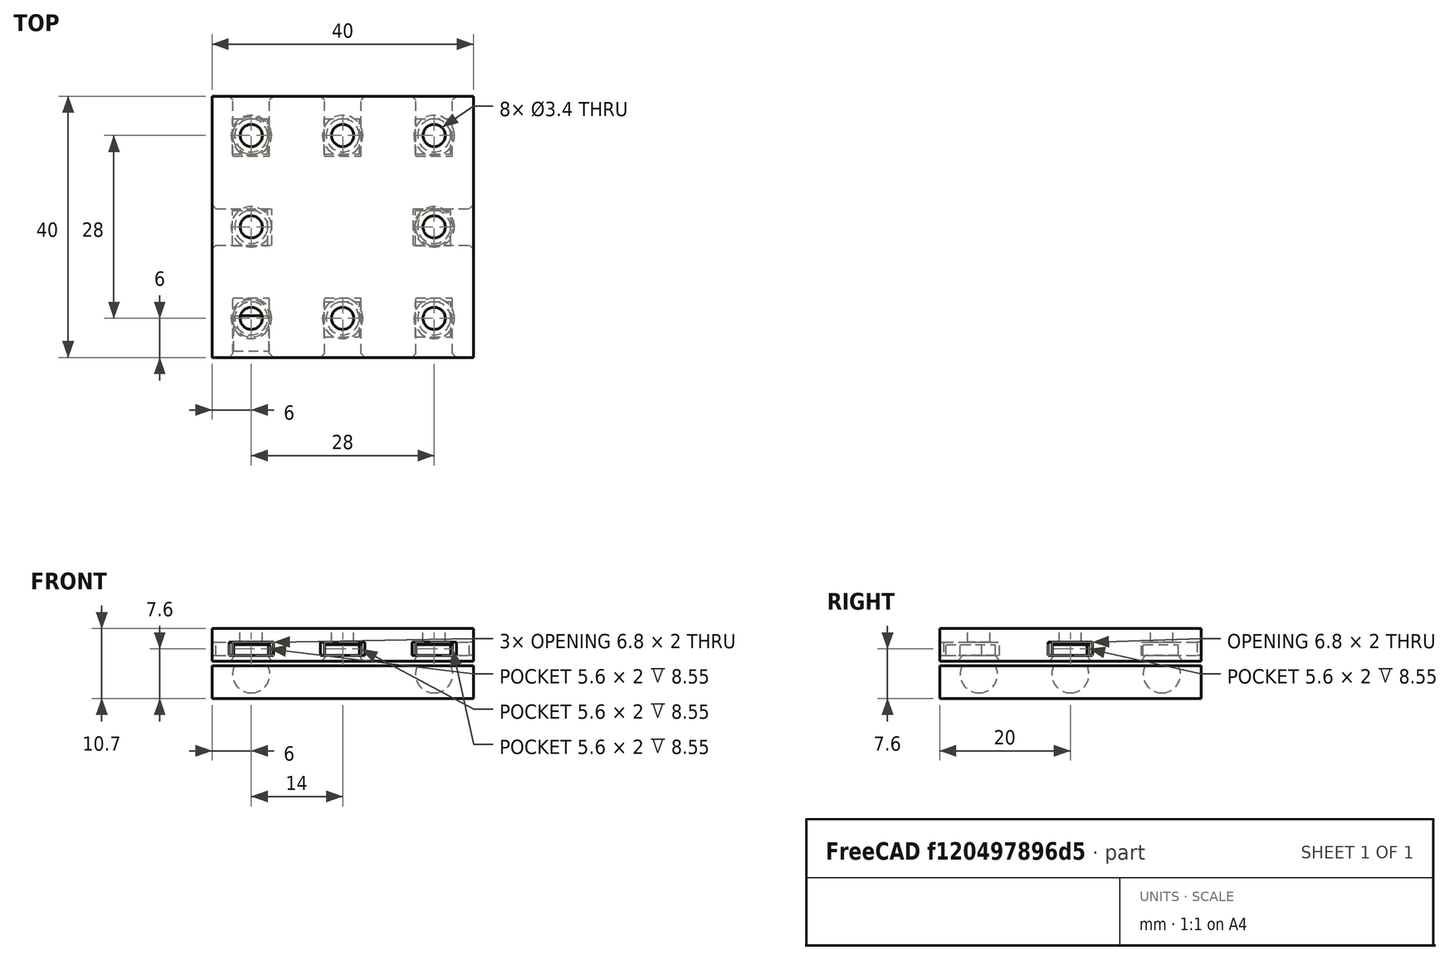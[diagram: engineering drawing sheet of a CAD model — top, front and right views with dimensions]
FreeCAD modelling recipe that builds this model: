
FCSTD DOCUMENT  (FreeCAD 0.17R13522 (Git))
Label: Face plates
License: All rights reserved
LicenseURL: http://en.wikipedia.org/wiki/All_rights_reserved
objects: Part::Box×18, Part::Sphere×11, Part::Cylinder×8, Part::MultiFuse×5, Part::Cut×4, Part::Chamfer×4
note: 50 computed .brp shape members not serialized (recipe doc carries the construction recipe); baked Part::Feature solids carry a one-line shape summary decoded from their .brp

FEATURE [Part::Box] Box  label="Cube"
  AttacherType = Attacher::AttachEngine3D
  Height = 5
  Length = 40
  Placement = pos=(0,0,-2) rot=(0,0,1;0rad)
  Width = 40
FEATURE [Part::Sphere] Sphere  label="Mag Hole"
  Angle1 = -90
  Angle2 = 90
  Angle3 = 360
  AttacherType = Attacher::AttachEngine3D
  Placement = pos=(6,6,1.7) rot=(0,0,1;0rad)
  Radius = 2.85
FEATURE [Part::Sphere] Sphere005  label="Mag Hole 2"
  Angle1 = -90
  Angle2 = 90
  Angle3 = 360
  AttacherType = Attacher::AttachEngine3D
  Placement = pos=(34,20,1.7) rot=(0,0,1;0rad)
  Radius = 2.85
FEATURE [Part::Sphere] Sphere003  label="Mag Hole 3"
  Angle1 = -90
  Angle2 = 90
  Angle3 = 360
  AttacherType = Attacher::AttachEngine3D
  Placement = pos=(6,34,1.7) rot=(0,0,1;0rad)
  Radius = 2.85
FEATURE [Part::Box] Box001  label="Cube001"
  AttacherType = Attacher::AttachEngine3D
  Height = 5
  Length = 40
  Placement = pos=(0,0,3.7) rot=(0,0,1;0rad)
  Width = 40
FEATURE [Part::Box] Box002  label="Square Nut"
  AttacherType = Attacher::AttachEngine3D
  Height = 1.65
  Length = 5.4
  Placement = pos=(3.3,1,4.6) rot=(0,0,1;0rad)
  Width = 5.4
FEATURE [Part::Box] Box003  label="Square Nut001"
  AttacherType = Attacher::AttachEngine3D
  Height = 1.65
  Length = 5.4
  Placement = pos=(31.15,17.15,4.6) rot=(0,0,1;0rad)
  Width = 5.4
FEATURE [Part::Box] Box005  label="Square Nut002"
  AttacherType = Attacher::AttachEngine3D
  Height = 1.65
  Length = 5.4
  Placement = pos=(3.15,31.15,4.6) rot=(0,0,1;0rad)
  Width = 5.4
FEATURE [Part::Box] Box006  label="Square Nut003"
  AttacherType = Attacher::AttachEngine3D
  Height = 1.65
  Length = 5.4
  Placement = pos=(17.15,3.15,4.6) rot=(0,0,1;0rad)
  Width = 5.4
FEATURE [Part::Box] Box007  label="Square Nut004"
  AttacherType = Attacher::AttachEngine3D
  Height = 1.65
  Length = 5.4
  Placement = pos=(17.15,31.15,4.6) rot=(0,0,1;0rad)
  Width = 5.4
FEATURE [Part::Box] Box008  label="Square Nut005"
  AttacherType = Attacher::AttachEngine3D
  Height = 1.65
  Length = 5.4
  Placement = pos=(31.15,3.15,4.6) rot=(0,0,1;0rad)
  Width = 5.4
FEATURE [Part::Box] Box009  label="Square Nut006"
  AttacherType = Attacher::AttachEngine3D
  Height = 1.65
  Length = 5.4
  Placement = pos=(31.15,31.15,4.6) rot=(0,0,1;0rad)
  Width = 5.4
FEATURE [Part::Box] Box010  label="Square Nut007"
  AttacherType = Attacher::AttachEngine3D
  Height = 1.65
  Length = 5.4
  Placement = pos=(3.15,17.15,4.6) rot=(0,0,1;0rad)
  Width = 5.4
FEATURE [Part::MultiFuse] Fusion  label="Square Nuts"
  Shapes = -> [Box008,Box007,Box006,Box003,Box005,Box009,Box010,Box002]
FEATURE [Part::Box] Box011  label="Square Nut Hole 008"
  AttacherType = Attacher::AttachEngine3D
  Height = 2
  Length = 5.6
  Placement = pos=(17.2,30.85,4.6) rot=(0,0,1;0rad)
  Width = 10
FEATURE [Part::Box] Box012  label="Square Nut Hole 009"
  AttacherType = Attacher::AttachEngine3D
  Height = 2
  Length = 5.6
  Placement = pos=(17.2,-0.85,4.6) rot=(0,0,1;0rad)
  Width = 10
FEATURE [Part::Box] Box013  label="Square Nut Hole 010"
  AttacherType = Attacher::AttachEngine3D
  Height = 2
  Length = 5.6
  Placement = pos=(31.2,-0.85,4.6) rot=(0,0,1;0rad)
  Width = 10
FEATURE [Part::Box] Box014  label="Square Nut Hole 011"
  AttacherType = Attacher::AttachEngine3D
  Height = 2
  Length = 10
  Placement = pos=(30.85,17.2,4.6) rot=(0,0,1;0rad)
  Width = 5.6
FEATURE [Part::Box] Box015  label="Square Nut Hole 012"
  AttacherType = Attacher::AttachEngine3D
  Height = 2
  Length = 5.6
  Placement = pos=(3.2,30.85,4.6) rot=(0,0,1;0rad)
  Width = 10
FEATURE [Part::Box] Box016  label="Square Nut Hole 013"
  AttacherType = Attacher::AttachEngine3D
  Height = 2
  Length = 5.6
  Placement = pos=(31.2,30.85,4.6) rot=(0,0,1;0rad)
  Width = 10
FEATURE [Part::Box] Box017  label="Square Nut Hole 014"
  AttacherType = Attacher::AttachEngine3D
  Height = 2
  Length = 10
  Placement = pos=(-0.85,17.2,4.6) rot=(0,0,1;0rad)
  Width = 5.6
FEATURE [Part::Box] Box018  label="Square Nut Hole 015"
  AttacherType = Attacher::AttachEngine3D
  Height = 2
  Length = 5.6
  Placement = pos=(3.2,-0.85,4.6) rot=(0,0,1;0rad)
  Width = 10
FEATURE [Part::MultiFuse] Fusion001  label="Square Nut Hole"
  Shapes = -> [Box013,Box014,Box016,Box012,Box017,Box015,Box018,Box011]
FEATURE [Part::Sphere] Sphere006  label="Nut Clearence1"
  Angle1 = -90
  Angle2 = 90
  Angle3 = 360
  AttacherType = Attacher::AttachEngine3D
  Placement = pos=(6,6,2.4) rot=(0,0,1;0rad)
  Radius = 3.35
FEATURE [Part::Sphere] Sphere007
  Angle1 = -90
  Angle2 = 90
  Angle3 = 360
  AttacherType = Attacher::AttachEngine3D
  Placement = pos=(34,20,2.4) rot=(0,0,1;0rad)
  Radius = 3.35
FEATURE [Part::Sphere] Sphere008
  Angle1 = -90
  Angle2 = 90
  Angle3 = 360
  AttacherType = Attacher::AttachEngine3D
  Placement = pos=(6,34,2.4) rot=(0,0,1;0rad)
  Radius = 3.35
FEATURE [Part::Sphere] Sphere001
  Angle1 = -90
  Angle2 = 90
  Angle3 = 360
  AttacherType = Attacher::AttachEngine3D
  Placement = pos=(34,6,2.4) rot=(0,0,1;0rad)
  Radius = 3.35
FEATURE [Part::Sphere] Sphere009
  Angle1 = -90
  Angle2 = 90
  Angle3 = 360
  AttacherType = Attacher::AttachEngine3D
  Placement = pos=(20,6,2.4) rot=(0,0,1;0rad)
  Radius = 3.35
FEATURE [Part::Sphere] Sphere010
  Angle1 = -90
  Angle2 = 90
  Angle3 = 360
  AttacherType = Attacher::AttachEngine3D
  Placement = pos=(20,34,2.4) rot=(0,0,1;0rad)
  Radius = 3.35
FEATURE [Part::Sphere] Sphere004
  Angle1 = -90
  Angle2 = 90
  Angle3 = 360
  AttacherType = Attacher::AttachEngine3D
  Placement = pos=(6,20,2.4) rot=(0,0,1;0rad)
  Radius = 3.35
FEATURE [Part::Sphere] Sphere002
  Angle1 = -90
  Angle2 = 90
  Angle3 = 360
  AttacherType = Attacher::AttachEngine3D
  Placement = pos=(34,34,2.4) rot=(0,0,1;0rad)
  Radius = 3.35
FEATURE [Part::Cylinder] Cylinder
  Angle = 360
  AttacherType = Attacher::AttachEngine3D
  Height = 10
  Placement = pos=(6,6,0) rot=(0,0,1;0rad)
  Radius = 1.7
FEATURE [Part::Cylinder] Cylinder001
  Angle = 360
  AttacherType = Attacher::AttachEngine3D
  Height = 10
  Placement = pos=(20,6,0) rot=(0,0,1;0rad)
  Radius = 1.7
FEATURE [Part::Cylinder] Cylinder002
  Angle = 360
  AttacherType = Attacher::AttachEngine3D
  Height = 10
  Placement = pos=(34,6,0) rot=(0,0,1;0rad)
  Radius = 1.7
FEATURE [Part::Cylinder] Cylinder003
  Angle = 360
  AttacherType = Attacher::AttachEngine3D
  Height = 10
  Placement = pos=(34,34,0) rot=(0,0,1;0rad)
  Radius = 1.7
FEATURE [Part::Cylinder] Cylinder004
  Angle = 360
  AttacherType = Attacher::AttachEngine3D
  Height = 10
  Placement = pos=(20,34,0) rot=(0,0,1;0rad)
  Radius = 1.7
FEATURE [Part::Cylinder] Cylinder005
  Angle = 360
  AttacherType = Attacher::AttachEngine3D
  Height = 10
  Placement = pos=(6,34,0) rot=(0,0,1;0rad)
  Radius = 1.7
FEATURE [Part::Cylinder] Cylinder006
  Angle = 360
  AttacherType = Attacher::AttachEngine3D
  Height = 10
  Placement = pos=(6,20,0) rot=(0,0,1;0rad)
  Radius = 1.7
FEATURE [Part::Cylinder] Cylinder007
  Angle = 360
  AttacherType = Attacher::AttachEngine3D
  Height = 10
  Placement = pos=(34,20,0) rot=(0,0,1;0rad)
  Radius = 1.7
FEATURE [Part::MultiFuse] Fusion002
  Shapes = -> [Cylinder,Cylinder004,Cylinder007,Cylinder005,Cylinder006,Cylinder001,Cylinder002,Cylinder003]
FEATURE [Part::MultiFuse] Fusion003
  Shapes = -> [Sphere007,Sphere008,Sphere006,Sphere009,Sphere001,Sphere010,Sphere004,Sphere002]
FEATURE [Part::Cut] Cut
  Base = -> Box001
  Tool = -> Fusion001
FEATURE [Part::Cut] Cut001
  Base = -> Cut
  Tool = -> Fusion003
FEATURE [Part::Cut] Cut002
  Base = -> Cut001
  Tool = -> Fusion002
FEATURE [Part::MultiFuse] Fusion004
  Shapes = -> [Sphere,Sphere005,Sphere003]
FEATURE [Part::Cut] Cut003
  Base = -> Box
  Tool = -> Fusion004
FEATURE [Part::Chamfer] Chamfer
  Base = -> Cut002
  Edges = 1 edges r=0.6: [Edge50]
FEATURE [Part::Chamfer] Chamfer001
  Base = -> Chamfer
  Edges = 5 edges r=0.6: [Edge4,Edge12,Edge14,Edge16,Edge18]
FEATURE [Part::Chamfer] Chamfer002
  Base = -> Chamfer001
  Edges = 4 edges r=0.6: [Edge57,Edge59,Edge63,Edge65]
FEATURE [Part::Chamfer] Chamfer003
  Base = -> Chamfer002
  Edges = 6 edges r=0.6: [Edge31,Edge33,Edge35,Edge37,Edge39,Edge41]
